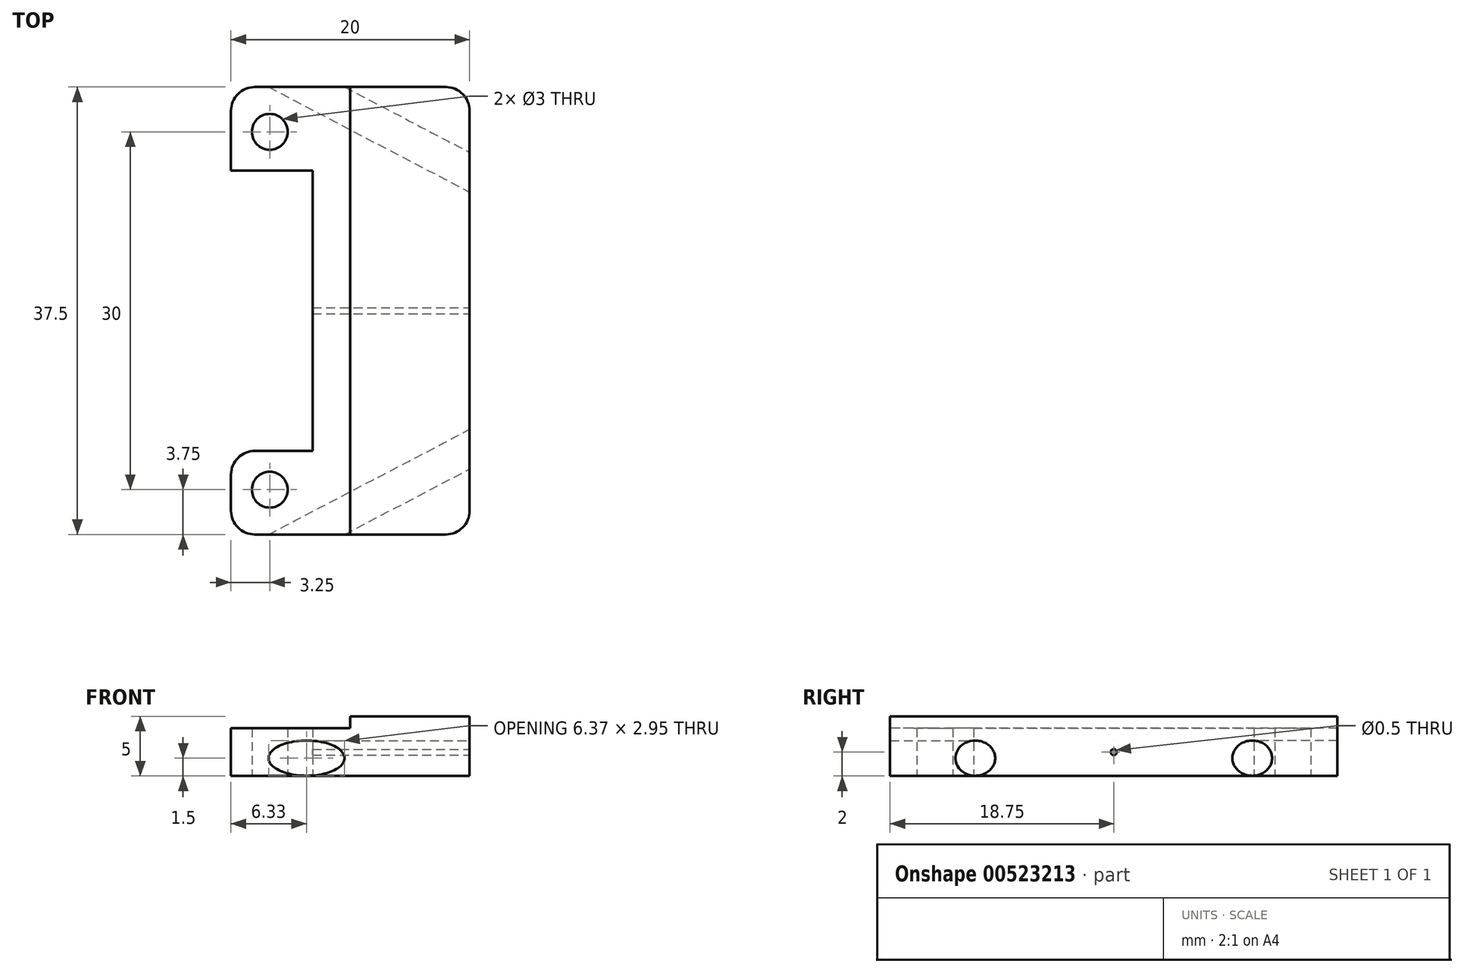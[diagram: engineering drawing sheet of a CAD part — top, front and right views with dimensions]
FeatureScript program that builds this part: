
annotation { "Feature Type Name" : "Feature", "Feature Type Description" : "" }
export const myFeature = defineFeature(function(context is Context, id is Id, definition is map)
    precondition{}
    {
        {
            var Q0;
            Q0=qCreatedBy(makeId("Top.planeOp"),FACE);
            var sketch = newSketch(context, id + "F0", { "sketchPlane" : qUnion([Q0])});
            skLineSegment(sketch, "E0.bottom", {"start": v(-10, -18.75) * mm, "end": v(10, -18.75) * mm});
            skLineSegment(sketch, "E0.top", {"start": v(-10, 18.75) * mm, "end": v(10, 18.75) * mm});
            skLineSegment(sketch, "E0.left", {"start": v(-10, -18.75) * mm, "end": v(-10, 18.75) * mm});
            skLineSegment(sketch, "E0.right", {"start": v(10, -18.75) * mm, "end": v(10, 18.75) * mm});
            skPoint(sketch, "E0.middle", {"position": v(0, 0) * mm});
            skSolve(sketch);
        }
        {
            var Q0;
            Q0 = qSketchRegion(id + "F0", true);
            extrude(context, id + "F1", {"entities" : qUnion([Q0]), "depth" : 5 * mm, "offsetDistance" : 25 * mm});
        }
        {
            var Q0;
            Q0=makeQuery(id+"F1.opExtrude","CAP_FACE",FACE,{"disambiguationData":[OSD([sQuery(id+"F0.wireOp",EDGE,"E0.bottom"),sQuery(id+"F0.wireOp",EDGE,"E0.top"),sQuery(id+"F0.wireOp",EDGE,"E0.left"),sQuery(id+"F0.wireOp",EDGE,"E0.right")])],"isStart":false});
            var sketch = newSketch(context, id + "F2", { "sketchPlane" : qUnion([Q0])});
            skLineSegment(sketch, "E1.bottom", {"start": v(-10, 18.75) * mm, "end": v(0, 18.75) * mm});
            skLineSegment(sketch, "E1.top", {"start": v(-10, -18.75) * mm, "end": v(0, -18.75) * mm});
            skLineSegment(sketch, "E1.left", {"start": v(-10, 18.75) * mm, "end": v(-10, -18.75) * mm});
            skLineSegment(sketch, "E1.right", {"start": v(0, 18.75) * mm, "end": v(0, -18.75) * mm});
            skSolve(sketch);
        }
        {
            var Q0;
            Q0 = qSketchRegion(id + "F2", true);
            extrude(context, id + "F3", {"entities" : qUnion([Q0]), "operationType" : NewBodyOperationType.REMOVE, "oppositeDirection" : true, "depth" : 1 * mm, "offsetDistance" : 25 * mm});
        }
        {
            var Q0;
            Q0=qCreatedBy(makeId("Top.planeOp"),FACE);
            var sketch = newSketch(context, id + "F4", { "sketchPlane" : qUnion([Q0])});
            skLineSegment(sketch, "E2.bottom", {"start": v(-6.75, -15) * mm, "end": v(6.75, -15) * mm});
            skLineSegment(sketch, "E2.top", {"start": v(-6.75, 15) * mm, "end": v(6.75, 15) * mm});
            skLineSegment(sketch, "E2.left", {"start": v(-6.75, -15) * mm, "end": v(-6.75, 15) * mm});
            skLineSegment(sketch, "E2.right", {"start": v(6.75, -15) * mm, "end": v(6.75, 15) * mm});
            skPoint(sketch, "E2.middle", {"position": v(0, 0) * mm});
            skCircle(sketch, "E3", {"center": v(-6.75, -15) * mm, "radius": 1.5 * mm});
            skCircle(sketch, "E4", {"center": v(-6.75, 15) * mm, "radius": 1.5 * mm});
            skSolve(sketch);
        }
        {
            var Q0;
            Q0=sQuery(id+"F4.wireOp",VERTEX,"E2.left.start");
            var Q1;
            Q1=sQuery(id+"F4.wireOp",VERTEX,"E2.left.end");
            var Q2;
            Q2=makeQuery(id+"F1.opExtrude","SWEPT_BODY",BODY,{"disambiguationData":[OSD([sQuery(id+"F0.wireOp",EDGE,"E0.bottom"),sQuery(id+"F0.wireOp",EDGE,"E0.top"),sQuery(id+"F0.wireOp",EDGE,"E0.left"),sQuery(id+"F0.wireOp",EDGE,"E0.right")])]});
            hole(context, id + "F5", {"style" : HoleStyle.SIMPLE, "endStyle" : HoleEndStyle.THROUGH, "oppositeDirection" : true, "holeDiameter" : 3 * mm, "isTappedThrough" : true, "tappedDepth" : 12 * mm, "tapClearance" : 3, "locations" : qUnion([Q0, Q1]), "scope" : qUnion([Q2])});
        }
        {
            var Q0;
            Q0=qCreatedBy(makeId("Top.planeOp"),FACE);
            var sketch = newSketch(context, id + "F6", { "sketchPlane" : qUnion([Q0])});
            skLineSegment(sketch, "E5.bottom", {"start": v(-10, 11.75) * mm, "end": v(-3.17, 11.75) * mm});
            skLineSegment(sketch, "E5.top", {"start": v(-10, -11.75) * mm, "end": v(-3.17, -11.75) * mm});
            skLineSegment(sketch, "E5.left", {"start": v(-10, 11.75) * mm, "end": v(-10, -11.75) * mm});
            skLineSegment(sketch, "E5.right", {"start": v(-3.17, 11.75) * mm, "end": v(-3.17, -11.75) * mm});
            skSolve(sketch);
        }
        {
            var Q0;
            Q0 = qSketchRegion(id + "F6", true);
            extrude(context, id + "F7", {"entities" : qUnion([Q0]), "operationType" : NewBodyOperationType.REMOVE, "depth" : 6 * mm, "offsetDistance" : 25 * mm});
        }
        {
            var Q0;
            Q0=makeQuery(id+"F1.opExtrude","SWEPT_EDGE",EDGE,{"disambiguationData":[OSD([sQuery(id+"F0.wireOp",EDGE,"E0.bottom"),sQuery(id+"F0.wireOp",EDGE,"E0.left")])]});
            var Q1;
            Q1=makeQuery(id+"F1.opExtrude","SWEPT_EDGE",EDGE,{"disambiguationData":[OSD([sQuery(id+"F0.wireOp",EDGE,"E0.bottom"),sQuery(id+"F0.wireOp",EDGE,"E0.right")])]});
            var Q2;
            Q2=makeQuery(id+"F1.opExtrude","SWEPT_EDGE",EDGE,{"disambiguationData":[OSD([sQuery(id+"F0.wireOp",EDGE,"E0.top"),sQuery(id+"F0.wireOp",EDGE,"E0.right")])]});
            var Q3;
            Q3=makeQuery(id+"F1.opExtrude","SWEPT_EDGE",EDGE,{"disambiguationData":[OSD([sQuery(id+"F0.wireOp",EDGE,"E0.top"),sQuery(id+"F0.wireOp",EDGE,"E0.left")])]});
            var Q4;
            Q4=makeQuery(id+"F7.boolean.opBoolean","COPY",EDGE,{"derivedFrom":makeQuery(id+"F7.opExtrude","SWEPT_EDGE",EDGE,{"disambiguationData":[OSD([sQuery(id+"F6.wireOp",EDGE,"E5.top"),sQuery(id+"F6.wireOp",EDGE,"E5.left")])]})});
            var Q5;
            Q5=makeQuery(id+"F7.boolean.opBoolean","COPY",EDGE,{"derivedFrom":makeQuery(id+"F7.opExtrude","SWEPT_EDGE",EDGE,{"disambiguationData":[OSD([sQuery(id+"F6.wireOp",EDGE,"E5.bottom"),sQuery(id+"F6.wireOp",EDGE,"E5.left")])]})});
            fillet(context, id + "F8", {"entities" : qUnion([Q0, Q1, Q2, Q3, Q4, Q5]), "radius" : 2 * mm, "tangentPropagation" : true, "allowEdgeOverflow" : false});
        }
        {
            var Q0;
            Q0=qCreatedBy(makeId("Top.planeOp"),FACE);
            var sketch = newSketch(context, id + "F9", { "sketchPlane" : qUnion([Q0])});
            skLineSegment(sketch, "E6", {"start": v(-6.9, -16.77) * mm, "end": v(9.89, -8) * mm});
            skLineSegment(sketch, "E7", {"start": v(9.89, 8) * mm, "end": v(9.89, 0) * mm});
            skLineSegment(sketch, "E8", {"start": v(9.89, -8) * mm, "end": v(9.89, 0) * mm});
            skLineSegment(sketch, "E9", {"start": v(-8.53, 17.62) * mm, "end": v(9.89, 8) * mm});
            skLineSegment(sketch, "E10", {"start": v(-8.5, 21.28) * mm, "end": v(10, 11.6) * mm});
            skLineSegment(sketch, "E11", {"start": v(-7.77, -20.9) * mm, "end": v(10, -11.6) * mm});
            skLineSegment(sketch, "E12", {"start": v(1.4, -3.95) * mm, "end": v(10.93, -22.2) * mm});
            skPoint(sketch, "E13", {"position": v(4.88, -10.62) * mm});
            skLineSegment(sketch, "E14", {"start": v(9.3, 11.97) * mm, "end": v(10, 13.3) * mm});
            skPoint(sketch, "E15", {"position": v(6.39, -13.5) * mm});
            skSolve(sketch);
        }
        {
            var Q0;
            Q0=sQuery(id+"F9.wireOp",EDGE,"E14");
            cPlane(context, id + "F10", {"entities" : qUnion([Q0]), "cplaneType" : CPlaneType.LINE_ANGLE, "offset" : 25 * mm, "angle" : 90 * degree, "width" : 150 * mm, "height" : 150 * mm});
        }
        {
            var Q0;
            Q0=qCreatedBy(id+"F10.planeOp",FACE);
            var Q1;
            Q1=qCreatedBy(id+"F10.planeOp",FACE);
            var Q2;
            Q2=qCreatedBy(id+"F10.planeOp",FACE);
            var sketch = newSketch(context, id + "F11", { "sketchPlane" : qUnion([Q0, Q1, Q2])});
            skLineSegment(sketch, "E16", {"start": v(14.92, 0) * mm, "end": v(14.92, 1.5) * mm});
            skPoint(sketch, "E17", {"position": v(14.92, 1.5) * mm});
            skSolve(sketch);
        }
        {
            var Q0;
            Q0=qCreatedBy(id+"F10.planeOp",FACE);
            var Q1;
            Q1=qCreatedBy(id+"F10.planeOp",FACE);
            var sketch = newSketch(context, id + "F12", { "sketchPlane" : qUnion([Q0, Q1])});
            skCircle(sketch, "E18", {"center": v(14.92, 1.5) * mm, "radius": 1.48 * mm});
            skSolve(sketch);
        }
        {
            var Q0;
            Q0 = qSketchRegion(id + "F12", true);
            extrude(context, id + "F13", {"entities" : qUnion([Q0]), "operationType" : NewBodyOperationType.REMOVE, "endBound" : BoundingType.SYMMETRIC, "oppositeDirection" : true, "depth" : 52 * mm, "offsetDistance" : 25 * mm});
        }
        {
            var Q0;
            Q0=sQuery(id+"F9.wireOp",EDGE,"E12");
            cPlane(context, id + "F14", {"entities" : qUnion([Q0]), "cplaneType" : CPlaneType.LINE_ANGLE, "offset" : 25 * mm, "angle" : 90 * degree, "width" : 150 * mm, "height" : 150 * mm});
        }
        {
            var Q0;
            Q0=qCreatedBy(id+"F14.planeOp",FACE);
            var Q1;
            Q1=qCreatedBy(id+"F14.planeOp",FACE);
            var sketch = newSketch(context, id + "F15", { "sketchPlane" : qUnion([Q0, Q1])});
            skLineSegment(sketch, "E19", {"start": v(-14.92, 0) * mm, "end": v(-14.92, 1.5) * mm});
            skPoint(sketch, "E20", {"position": v(-14.92, 1.5) * mm});
            skSolve(sketch);
        }
        {
            var Q0;
            Q0=qCreatedBy(id+"F14.planeOp",FACE);
            var Q1;
            Q1=qCreatedBy(id+"F14.planeOp",FACE);
            var Q2;
            Q2=qCreatedBy(id+"F14.planeOp",FACE);
            var Q3;
            Q3=qCreatedBy(id+"F14.planeOp",FACE);
            var Q4;
            Q4=qCreatedBy(id+"F14.planeOp",FACE);
            var sketch = newSketch(context, id + "F16", { "sketchPlane" : qUnion([Q0, Q1, Q2, Q3, Q4])});
            skCircle(sketch, "E21", {"center": v(-14.92, 1.5) * mm, "radius": 1.48 * mm});
            skSolve(sketch);
        }
        {
            var Q0;
            Q0 = qSketchRegion(id + "F16", true);
            extrude(context, id + "F17", {"entities" : qUnion([Q0]), "operationType" : NewBodyOperationType.REMOVE, "endBound" : BoundingType.SYMMETRIC, "oppositeDirection" : true, "depth" : 55 * mm, "offsetDistance" : 25 * mm});
        }
        {
            var Q0;
            Q0=makeQuery(id+"F1.opExtrude","SWEPT_FACE",FACE,{"disambiguationData":[OSD([sQuery(id+"F0.wireOp",EDGE,"E0.right")])]});
            var Q1;
            Q1=makeQuery(id+"F1.opExtrude","SWEPT_FACE",FACE,{"disambiguationData":[OSD([sQuery(id+"F0.wireOp",EDGE,"E0.right")])]});
            var sketch = newSketch(context, id + "F18", { "sketchPlane" : qUnion([Q0, Q1])});
            skLineSegment(sketch, "E22", {"start": v(0, 0) * mm, "end": v(0, 2) * mm});
            skPoint(sketch, "E23", {"position": v(0, 2) * mm});
            skSolve(sketch);
        }
        {
            var Q0;
            {var subQ0=sQuery(id+"F0.wireOp",EDGE,"E0.right");Q0=makeQuery(id+"F18.imprint","IMPRINT",FACE,{"disambiguationData":[TD([[makeQuery(id+"F18.imprint","IMPRINT",EDGE,{"derivedFrom":makeQuery(id+"F1.opExtrude","CAP_EDGE",EDGE,{"disambiguationData":[OSD([subQ0])],"isStart":false})}),-1.0]])]});}
            var Q1;
            {var subQ0=sQuery(id+"F0.wireOp",EDGE,"E0.right");Q1=makeQuery(id+"F18.imprint","IMPRINT",FACE,{"disambiguationData":[TD([[makeQuery(id+"F18.imprint","IMPRINT",EDGE,{"derivedFrom":makeQuery(id+"F1.opExtrude","CAP_EDGE",EDGE,{"disambiguationData":[OSD([subQ0])],"isStart":false})}),-1.0]])]});}
            var sketch = newSketch(context, id + "F19", { "sketchPlane" : qUnion([Q0, Q1])});
            skCircle(sketch, "E24", {"center": v(0, 2) * mm, "radius": 0.25 * mm});
            skSolve(sketch);
        }
        {
            var Q0;
            Q0 = qSketchRegion(id + "F19", true);
            extrude(context, id + "F20", {"entities" : qUnion([Q0]), "operationType" : NewBodyOperationType.REMOVE, "endBound" : BoundingType.SYMMETRIC, "oppositeDirection" : true, "depth" : 55 * mm, "offsetDistance" : 25 * mm});
        }
    });
